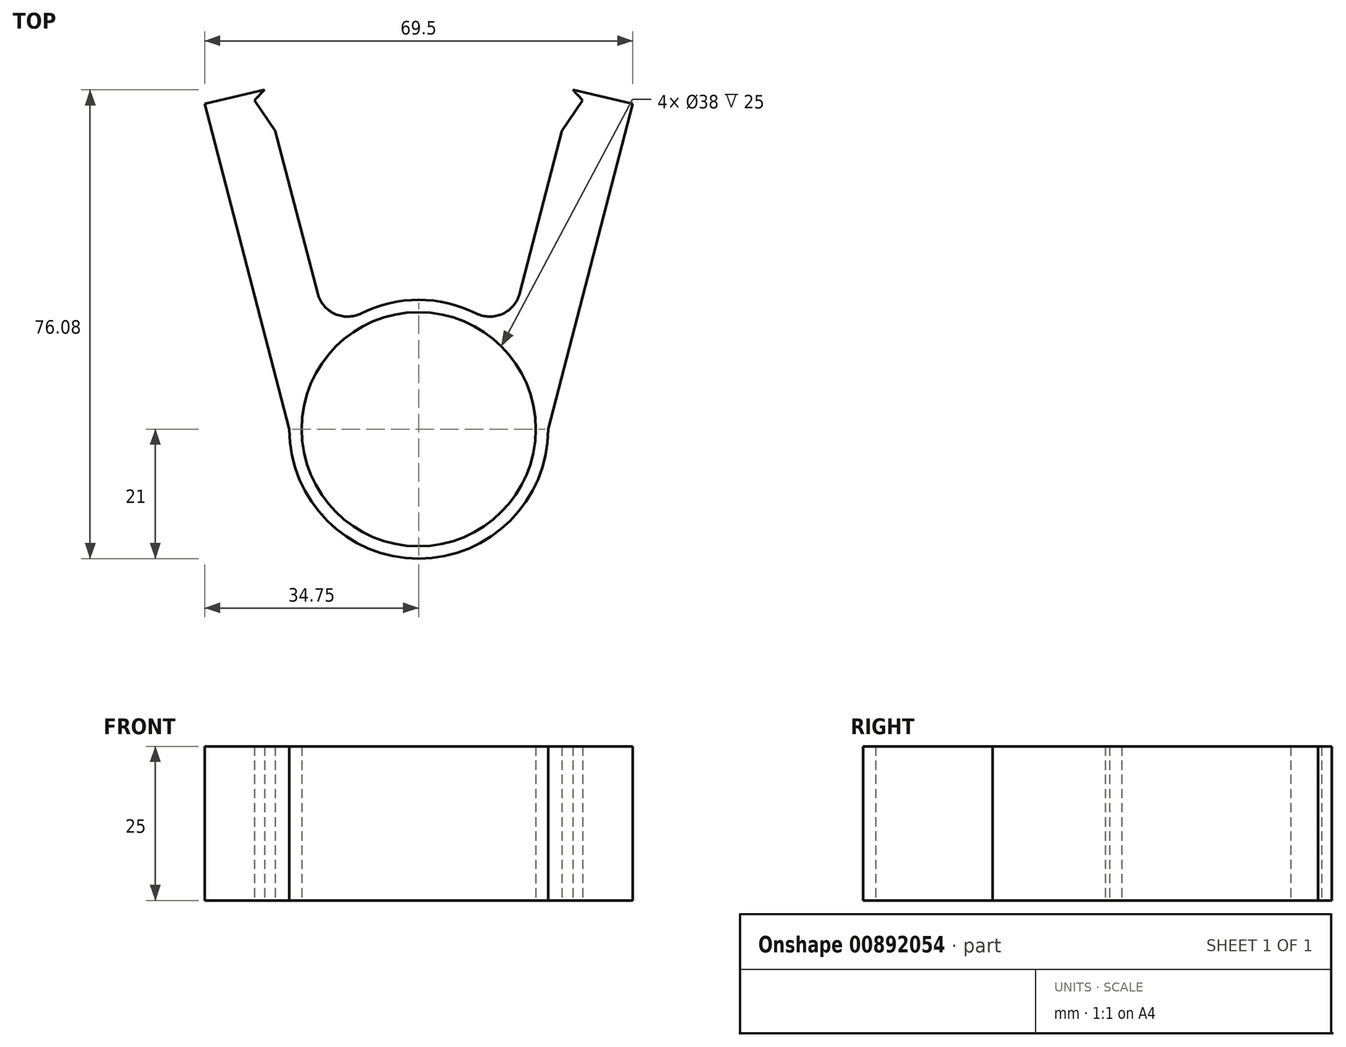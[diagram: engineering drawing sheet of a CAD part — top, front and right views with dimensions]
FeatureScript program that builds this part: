
annotation { "Feature Type Name" : "Feature", "Feature Type Description" : "" }
export const myFeature = defineFeature(function(context is Context, id is Id, definition is map)
    precondition{}
    {
        {
            var Q0;
            Q0=qCreatedBy(makeId("Top.planeOp"),FACE);
            var sketch = newSketch(context, id + "F0", { "sketchPlane" : qUnion([Q0])});
            skArc(sketch, "E0", {"start": v(-21, 0) * mm, "mid": v(0, -21) * mm, "end": v(21, 0) * mm});
            skLineSegment(sketch, "E1.top", {"start": v(32.31, 53.41) * mm, "end": v(34.75, 52.84) * mm});
            skLineSegment(sketch, "E1.left", {"start": v(21, 0) * mm, "end": v(34.75, 52.84) * mm});
            skLineSegment(sketch, "E1.right", {"start": v(14.6, 15.1) * mm, "end": v(23.26, 48.41) * mm});
            skLineSegment(sketch, "E2.MirrorCS", {"start": v(-14.6, 15.1) * mm, "end": v(-23.26, 48.41) * mm});
            skLineSegment(sketch, "E3.MirrorCS", {"start": v(-32.31, 53.41) * mm, "end": v(-34.75, 52.84) * mm});
            skLineSegment(sketch, "E4.MirrorCS", {"start": v(-21, 0) * mm, "end": v(-34.75, 52.84) * mm});
            skPoint(sketch, "E5.MirrorCS.end.orphan", {"position": v(-11.2, 2.09) * mm});
            skPoint(sketch, "E5.MirrorCS.start.orphan", {"position": v(-21, 0) * mm});
            skPoint(sketch, "E1.bottom.end.orphan", {"position": v(11.2, 2.09) * mm});
            skArc(sketch, "E6.trimOffspring", {"start": v(14.6, 15.1) * mm, "mid": v(0, 21) * mm, "end": v(-14.6, 15.1) * mm});
            skCircle(sketch, "E7", {"center": v(0, 0) * mm, "radius": 19 * mm});
            skLineSegment(sketch, "E8", {"start": v(32.31, 53.41) * mm, "end": v(25, 55.08) * mm});
            skLineSegment(sketch, "E9", {"start": v(25, 55.08) * mm, "end": v(26.63, 53.41) * mm});
            skLineSegment(sketch, "E10", {"start": v(26.63, 53.41) * mm, "end": v(23.26, 48.41) * mm});
            skLineSegment(sketch, "E11.MirrorCS", {"start": v(-26.63, 53.41) * mm, "end": v(-23.26, 48.41) * mm});
            skLineSegment(sketch, "E12.MirrorCS", {"start": v(-25, 55.08) * mm, "end": v(-26.63, 53.41) * mm});
            skLineSegment(sketch, "E13.MirrorCS", {"start": v(-32.31, 53.41) * mm, "end": v(-25, 55.08) * mm});
            skSolve(sketch);
        }
        {
            var Q0;
            Q0=makeQuery(id+"F0.imprint","IMPRINT",FACE,{"disambiguationData":[TD([[makeQuery(id+"F0.imprint","IMPRINT",EDGE,{"derivedFrom":sQuery(id+"F0.wireOp",EDGE,"E0")}),1.0]])]});
            extrude(context, id + "F1", {"entities" : qUnion([Q0]), "endBound" : BoundingType.SYMMETRIC, "depth" : 25 * mm, "offsetDistance" : 25 * mm});
        }
        {
            var Q0;
            Q0=makeQuery(id+"F1.opExtrude","SWEPT_EDGE",EDGE,{"disambiguationData":[OSD([sQuery(id+"F0.wireOp",EDGE,"E2.MirrorCS"),sQuery(id+"F0.wireOp",EDGE,"E6.trimOffspring")])]});
            var Q1;
            Q1=makeQuery(id+"F1.opExtrude","SWEPT_EDGE",EDGE,{"disambiguationData":[OSD([sQuery(id+"F0.wireOp",EDGE,"E1.right"),sQuery(id+"F0.wireOp",EDGE,"E6.trimOffspring")])]});
            fillet(context, id + "F2", {"entities" : qUnion([Q0, Q1]), "radius" : 5 * mm, "tangentPropagation" : true, "allowEdgeOverflow" : false});
        }
    });
